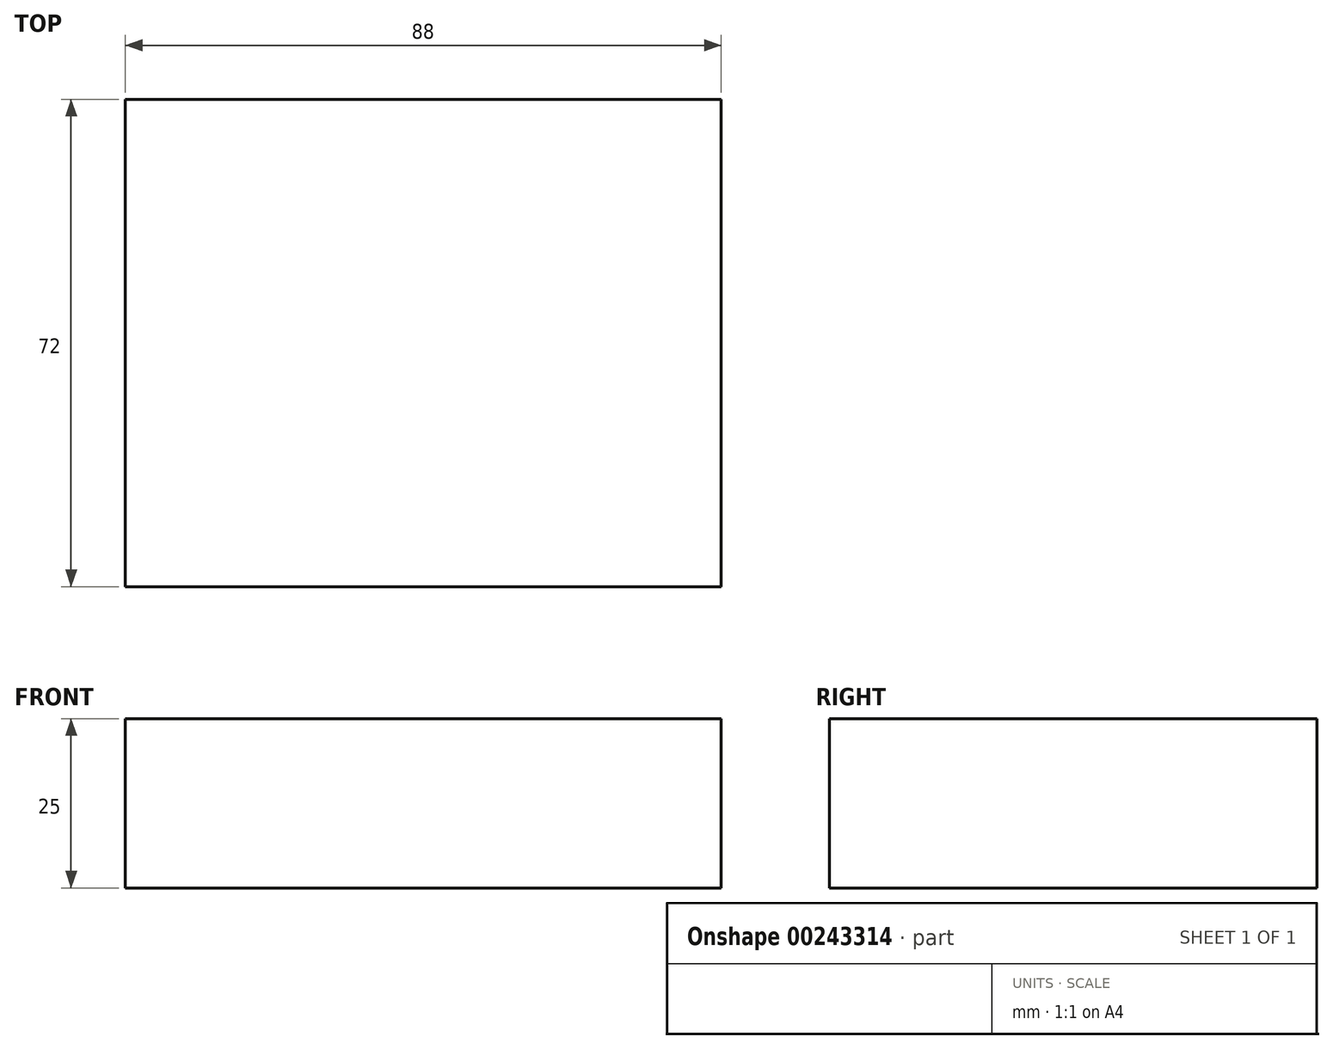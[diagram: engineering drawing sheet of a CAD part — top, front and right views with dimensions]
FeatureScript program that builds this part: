
annotation { "Feature Type Name" : "Feature", "Feature Type Description" : "" }
export const myFeature = defineFeature(function(context is Context, id is Id, definition is map)
    precondition{}
    {
        {
            var Q0;
            Q0=qCreatedBy(makeId("Top.planeOp"),FACE);
            var sketch = newSketch(context, id + "F0", { "sketchPlane" : qUnion([Q0])});
            skLineSegment(sketch, "E0.bottom", {"start": v(-44, 36) * mm, "end": v(44, 36) * mm});
            skLineSegment(sketch, "E0.top", {"start": v(-44, -36) * mm, "end": v(44, -36) * mm});
            skLineSegment(sketch, "E0.left", {"start": v(-44, 36) * mm, "end": v(-44, -36) * mm});
            skLineSegment(sketch, "E0.right", {"start": v(44, 36) * mm, "end": v(44, -36) * mm});
            skPoint(sketch, "E0.middle", {"position": v(0, 0) * mm});
            skSolve(sketch);
        }
        {
            var Q0;
            Q0 = qSketchRegion(id + "F0", true);
            extrude(context, id + "F1", {"entities" : qUnion([Q0]), "depth" : 25 * mm});
        }
    });
